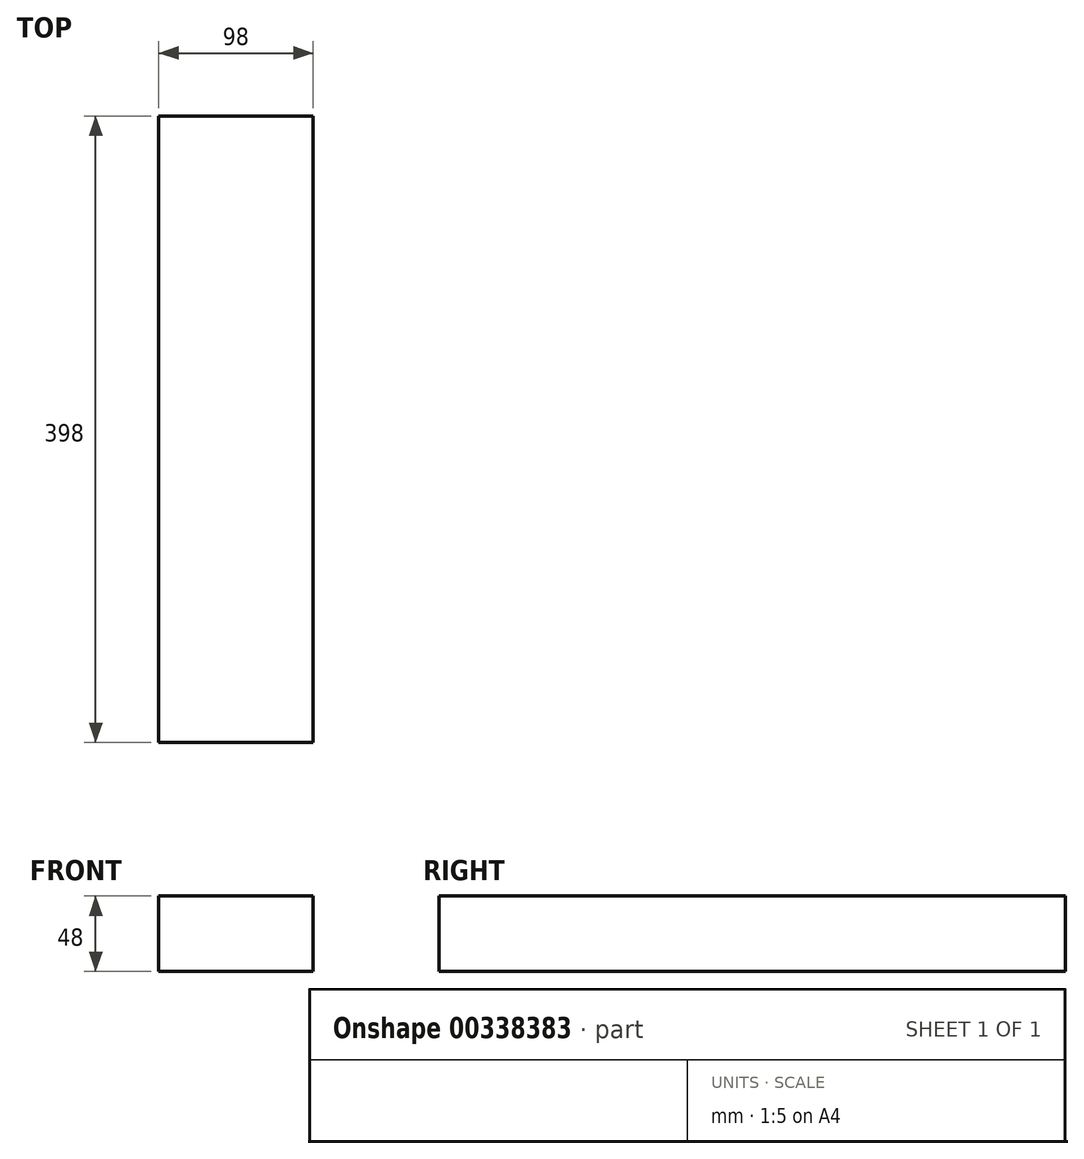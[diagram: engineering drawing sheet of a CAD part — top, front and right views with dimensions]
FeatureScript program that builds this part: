
annotation { "Feature Type Name" : "Feature", "Feature Type Description" : "" }
export const myFeature = defineFeature(function(context is Context, id is Id, definition is map)
    precondition{}
    {
        {
            var Q0;
            Q0=qCreatedBy(makeId("Front.planeOp"),FACE);
            var sketch = newSketch(context, id + "F0", { "sketchPlane" : qUnion([Q0])});
            skLineSegment(sketch, "E0.bottom", {"start": v(-49, -24) * mm, "end": v(49, -24) * mm});
            skLineSegment(sketch, "E0.top", {"start": v(-49, 24) * mm, "end": v(49, 24) * mm});
            skLineSegment(sketch, "E0.left", {"start": v(-49, -24) * mm, "end": v(-49, 24) * mm});
            skLineSegment(sketch, "E0.right", {"start": v(49, -24) * mm, "end": v(49, 24) * mm});
            skPoint(sketch, "E0.middle", {"position": v(0, 0) * mm});
            skSolve(sketch);
        }
        {
            var Q0;
            Q0=makeQuery(id+"F0.imprint","IMPRINT",FACE,{"disambiguationData":[TD([[makeQuery(id+"F0.imprint","IMPRINT",EDGE,{"derivedFrom":sQuery(id+"F0.wireOp",EDGE,"E0.bottom")}),1.0]])]});
            extrude(context, id + "F1", {"entities" : qUnion([Q0]), "depth" : 398 * mm});
        }
    });
